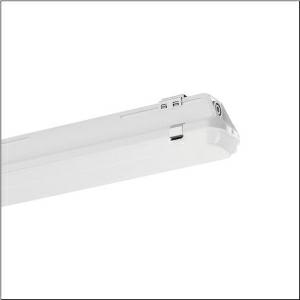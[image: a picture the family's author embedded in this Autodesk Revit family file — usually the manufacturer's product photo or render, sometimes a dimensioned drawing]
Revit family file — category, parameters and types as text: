
# Revit family: monsun_r__11_51fp107p4b0u_d884
name_source: partatom
category: Lighting Fixtures
units: mm (PartAtom-declared; Revit-internal decimal feet)

## family parameters
Cut with Voids When Loaded = No
Host = Face
Light Source = No
Part Type = Normal
Room Calculation Point = No
Round Connector Dimension = Use Diameter
Shared = No

## types (1)
- Monsun® 11 (1 x LED, 12070 lm, 62.4 W, 4000K)
    Apparent Load = 62 VA
    CIE Flux Codes = 47 76 93 94 100
    Color Rendering = 80
    Color Temperature = 4000K
    Default Elevation = 1800 mm
    Description = Monsun® 11, damp-proof luminaire, chain hanger, primary optical cover: enclosure, of PMMA, light emission: direct distribution, primary light characteristic: symmetric, installation type: suspended mounting, surface-mounted, horizontal mounting, vertical mounting, LED, rated luminous flux: 12.070lm, luminous efficacy: 193lm/W, light colour: 840, colour temperature: 4000K, control gear: ON/OFF, with terminal, 3-pole, max. 2.5mm², mains connection: 220..240V, AC, 50/60Hz, rated input power: 62W, luminaire housing, of glass-fibre reinforced polyester, uncoated, bright grey, incl. chain hanger, length: 1.590mm, width: 90mm, height: 88mm, clip for enclosure, of stainless steel (V2A), ceiling mounting element, of stainless steel (V2A), chain hanger, of stainless steel (V2A), protection rating (complete): IP66, insulation class (complete): insulation class I (protective earthing), certification: CE, ENEC, VDE, UKCA, protection symbol: D, impact resistance: IK04, permissible operating ambient temperature: -35..+35°C, standard: EN 50419, EN 60598-2-1, contact your sales advisor before using the luminaires in applications with unclear chemical exposure, large temperature fluctuations or condensation-forming humidity, LABS conformity tested according to VDMA 24364:2018-05, no direct snow, no direct sun, no direct rain, for indoor or canopied outdoor use, corresponds to IFS (International Featured Standards) requirements for safety and quality in the food industry, packaging unit: 1 piece
    Height = 89 mm
    Lamp = 1 x LED
    Lamp Light Flux = 12070 lm
    Lamp Power = 62.4 W
    Lamp count = 1
    Length = 1590 mm
    Luminous efficacy = 193 lm/W
    Manufacturer = Siteco
    ModVariant = No
    Model = 51FP107P4B0U
    Mounting Place = Ceiling
    Mounting Type = Surface mounted
    Number of Poles = 1
    OnlyDefault = Yes
    Power Factor = 1
    Product Name = Monsun® 11
    Product group = damp-proof luminaire
    ProductGroupID = 300
    Protection Class = Protection class I
    Protection Degree = IP 66
    RLX_Detail_Level = 1
    RLX_Emergency_Light_Flux = 0 lm
    RLX_Emergency_Type = 0
    RLX_Emergency_Type_DB = No
    RlxData = <blob elided: 88589 chars, md5=e65a8cdf>
    Socket = socket
    Standby Power = 0 W
    System Light Flux = 12070 lm
    System Power = 62 W
    Type Comments = Product without accessories
    Type Image = l_1349237.jpg
    URL = http://relux.com
    VarID = ---
    Voltage = 0 V
    Weight = 0.00 kg
    Width = 90 mm

## geometry (parser evidence)
native form markers: Blend x4, Sweep x13
no freeform markers — native parametric forms only
